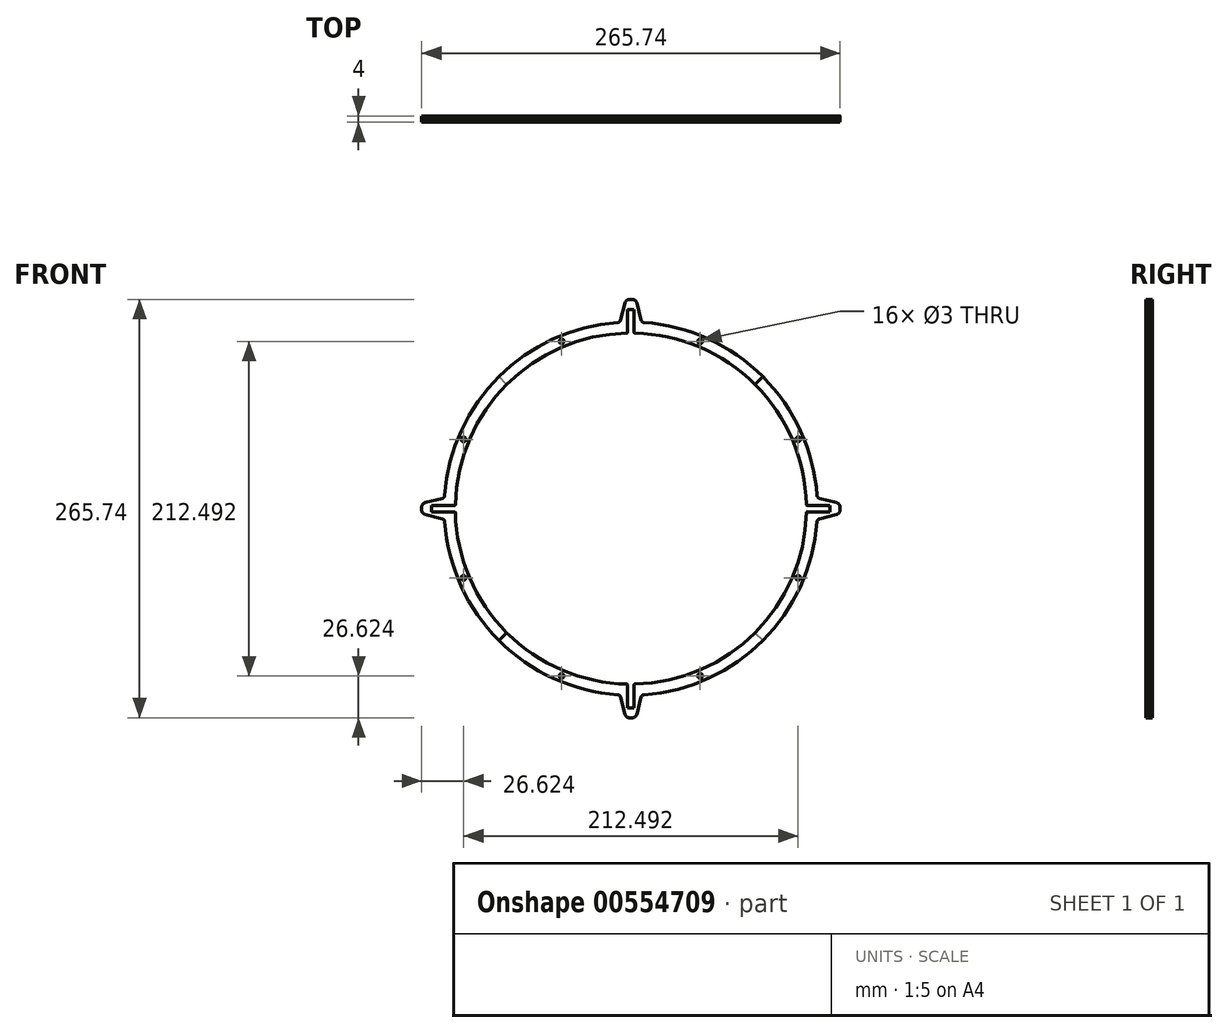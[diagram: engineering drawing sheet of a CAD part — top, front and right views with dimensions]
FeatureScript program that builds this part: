
annotation { "Feature Type Name" : "Feature", "Feature Type Description" : "" }
export const myFeature = defineFeature(function(context is Context, id is Id, definition is map)
    precondition{}
    {
        {
            var Q0;
            Q0=qCreatedBy(makeId("Front.planeOp"),FACE);
            var sketch = newSketch(context, id + "F0", { "sketchPlane" : qUnion([Q0])});
            skArc(sketch, "E0", {"start": v(-2.53, 111.47) * mm, "mid": v(-43.83, 102.52) * mm, "end": v(-78.84, 78.84) * mm});
            skArc(sketch, "E1", {"start": v(-8.32, 118.2) * mm, "mid": v(-49.16, 107.82) * mm, "end": v(-83.8, 83.8) * mm});
            skLineSegment(sketch, "E2", {"start": v(0, 0) * mm, "end": v(0, 308.78) * mm, "construction": true});
            skLineSegment(sketch, "E3", {"start": v(0, 0) * mm, "end": v(-78.84, 78.84) * mm, "construction": true});
            skLineSegment(sketch, "E4.bottom", {"start": v(0, 126.5) * mm, "end": v(2.18, 126.5) * mm});
            skLineSegment(sketch, "E5.bottom", {"start": v(-0.88, 132.87) * mm, "end": v(0.88, 132.87) * mm});
            skPoint(sketch, "E5.middle", {"position": v(0, 118.5) * mm});
            skLineSegment(sketch, "E6", {"start": v(-3.8, 130.6) * mm, "end": v(-6.52, 119.72) * mm});
            skLineSegment(sketch, "E7.MirrorCS", {"start": v(3.8, 130.6) * mm, "end": v(6.52, 119.72) * mm});
            skPoint(sketch, "E8.visualSharp", {"position": v(-3.23, 132.87) * mm});
            skArc(sketch, "E8.filletArc", {"start": v(-0.88, 132.87) * mm, "mid": v(-2.73, 132.23) * mm, "end": v(-3.8, 130.6) * mm});
            skPoint(sketch, "E9.visualSharp", {"position": v(3.23, 132.87) * mm});
            skArc(sketch, "E9.filletArc", {"start": v(3.8, 130.6) * mm, "mid": v(2.73, 132.23) * mm, "end": v(0.88, 132.87) * mm});
            skPoint(sketch, "E10.visualSharp", {"position": v(-1.55, 111.49) * mm});
            skPoint(sketch, "E11.visualSharp", {"position": v(1.55, 111.49) * mm});
            skPoint(sketch, "E12.visualSharp", {"position": v(-6.87, 118.3) * mm});
            skArc(sketch, "E12.filletArc", {"start": v(-8.32, 118.2) * mm, "mid": v(-7.17, 118.67) * mm, "end": v(-6.52, 119.72) * mm});
            skPoint(sketch, "E13.visualSharp", {"position": v(6.87, 118.3) * mm});
            skArc(sketch, "E13.filletArc", {"start": v(6.52, 119.72) * mm, "mid": v(7.17, 118.67) * mm, "end": v(8.32, 118.2) * mm});
            skLineSegment(sketch, "E14", {"start": v(0, 0) * mm, "end": v(-42.67, 103.01) * mm, "construction": true});
            skArc(sketch, "E15", {"start": v(83.8, 83.8) * mm, "mid": v(49.16, 107.82) * mm, "end": v(8.32, 118.2) * mm});
            skLineSegment(sketch, "E16", {"start": v(78.84, 78.84) * mm, "end": v(204.66, 204.66) * mm, "construction": true});
            skLineSegment(sketch, "E17", {"start": v(-83.8, 83.8) * mm, "end": v(-276.7, 276.7) * mm, "construction": true});
            skLineSegment(sketch, "E18", {"start": v(-78.84, 78.84) * mm, "end": v(-83.8, 83.8) * mm, "construction": true});
            skArc(sketch, "E19.trimOffspring", {"start": v(78.84, 78.84) * mm, "mid": v(43.83, 102.52) * mm, "end": v(2.53, 111.47) * mm});
            skLineSegment(sketch, "E20.3.6", {"start": v(78.84, 78.84) * mm, "end": v(83.8, 83.8) * mm, "construction": true});
            skPoint(sketch, "E21", {"position": v(-44, 106.25) * mm});
            skCircle(sketch, "E22", {"center": v(-44, 106.25) * mm, "radius": 1.5 * mm});
            skCircle(sketch, "E23.7.0", {"center": v(44, 106.25) * mm, "radius": 1.5 * mm});
            skLineSegment(sketch, "E24", {"start": v(83.8, 83.8) * mm, "end": v(78.84, 78.84) * mm});
            skLineSegment(sketch, "E25", {"start": v(-83.8, 83.8) * mm, "end": v(-78.84, 78.84) * mm});
            skPoint(sketch, "E26.orphan", {"position": v(-0.92, 126.5) * mm});
            skLineSegment(sketch, "E27.bottom", {"start": v(-2.05, 126.5) * mm, "end": v(2.05, 126.5) * mm});
            skLineSegment(sketch, "E27.left", {"start": v(-2.05, 126.5) * mm, "end": v(-2.05, 111.97) * mm});
            skLineSegment(sketch, "E27.right", {"start": v(2.05, 126.5) * mm, "end": v(2.05, 111.97) * mm});
            skLineSegment(sketch, "E28", {"start": v(-2.53, 111.47) * mm, "end": v(-2.52, 111.47) * mm});
            skPoint(sketch, "E29.visualSharp", {"position": v(-2.05, 111.5) * mm});
            skArc(sketch, "E29.filletArc", {"start": v(-2.52, 111.47) * mm, "mid": v(-2.19, 111.63) * mm, "end": v(-2.05, 111.97) * mm});
            skLineSegment(sketch, "E30.MirrorCS", {"start": v(2.53, 111.47) * mm, "end": v(2.52, 111.47) * mm});
            skArc(sketch, "E31.MirrorCS", {"start": v(2.52, 111.47) * mm, "mid": v(2.19, 111.63) * mm, "end": v(2.05, 111.97) * mm});
            skPoint(sketch, "E32.MirrorP", {"position": v(2.05, 111.5) * mm});
            skLineSegment(sketch, "E33.trimOffspring", {"start": v(-45.35, 109.48) * mm, "end": v(-110.65, 267.13) * mm, "construction": true});
            skPoint(sketch, "E34.1.0", {"position": v(-126.5, -0.92) * mm});
            skArc(sketch, "E34.1.1", {"start": v(-78.84, 78.84) * mm, "mid": v(-102.52, 43.83) * mm, "end": v(-111.47, 2.53) * mm});
            skPoint(sketch, "E34.1.2", {"position": v(-111.49, -1.55) * mm});
            skArc(sketch, "E34.1.3", {"start": v(-111.47, -2.53) * mm, "mid": v(-102.52, -43.83) * mm, "end": v(-78.84, -78.84) * mm});
            skPoint(sketch, "E34.1.4", {"position": v(-118.3, -6.87) * mm});
            skPoint(sketch, "E34.1.5", {"position": v(-111.5, 2.05) * mm});
            skPoint(sketch, "E34.1.6", {"position": v(-118.5, 0) * mm});
            skPoint(sketch, "E34.1.7", {"position": v(-111.5, -2.05) * mm});
            skPoint(sketch, "E34.1.8", {"position": v(-132.87, -3.23) * mm});
            skPoint(sketch, "E34.1.9", {"position": v(-111.49, 1.55) * mm});
            skArc(sketch, "E34.1.10", {"start": v(-118.2, -8.32) * mm, "mid": v(-107.82, -49.16) * mm, "end": v(-83.8, -83.8) * mm});
            skPoint(sketch, "E34.1.11", {"position": v(-132.87, 3.23) * mm});
            skPoint(sketch, "E34.1.12", {"position": v(-106.25, -44) * mm});
            skArc(sketch, "E34.1.13", {"start": v(-83.8, 83.8) * mm, "mid": v(-107.82, 49.16) * mm, "end": v(-118.2, 8.32) * mm});
            skPoint(sketch, "E34.1.14", {"position": v(-118.3, 6.87) * mm});
            skLineSegment(sketch, "E34.1.15", {"start": v(-126.5, -2.05) * mm, "end": v(-111.97, -2.05) * mm});
            skPoint(sketch, "E34.1.16", {"position": v(-111.49, 1.55) * mm});
            skCircle(sketch, "E34.1.17", {"center": v(-106.25, 44) * mm, "radius": 1.5 * mm});
            skLineSegment(sketch, "E34.1.18", {"start": v(-130.6, 3.8) * mm, "end": v(-119.72, 6.52) * mm});
            skLineSegment(sketch, "E34.1.19", {"start": v(-126.5, 2.05) * mm, "end": v(-111.97, 2.05) * mm});
            skLineSegment(sketch, "E34.1.20", {"start": v(-130.6, -3.8) * mm, "end": v(-119.72, -6.52) * mm});
            skCircle(sketch, "E34.1.21", {"center": v(-106.25, -44) * mm, "radius": 1.5 * mm});
            skLineSegment(sketch, "E34.1.22", {"start": v(-132.87, -0.88) * mm, "end": v(-132.87, 0.88) * mm});
            skArc(sketch, "E34.1.23", {"start": v(-118.2, -8.32) * mm, "mid": v(-118.67, -7.17) * mm, "end": v(-119.72, -6.52) * mm});
            skArc(sketch, "E34.1.24", {"start": v(-130.6, 3.8) * mm, "mid": v(-132.23, 2.73) * mm, "end": v(-132.87, 0.88) * mm});
            skArc(sketch, "E34.1.25", {"start": v(-132.87, -0.88) * mm, "mid": v(-132.23, -2.73) * mm, "end": v(-130.6, -3.8) * mm});
            skArc(sketch, "E34.1.26", {"start": v(-119.72, 6.52) * mm, "mid": v(-118.67, 7.17) * mm, "end": v(-118.2, 8.32) * mm});
            skLineSegment(sketch, "E34.1.28", {"start": v(-126.5, -2.05) * mm, "end": v(-126.5, 2.05) * mm});
            skLineSegment(sketch, "E34.1.29", {"start": v(-126.5, 0) * mm, "end": v(-126.5, 2.18) * mm});
            skLineSegment(sketch, "E34.1.30", {"start": v(-78.84, -78.84) * mm, "end": v(-83.8, -83.8) * mm, "construction": true});
            skLineSegment(sketch, "E34.1.32", {"start": v(-78.84, -78.84) * mm, "end": v(-83.8, -83.8) * mm, "construction": true});
            skLineSegment(sketch, "E34.1.34", {"start": v(-83.8, -83.8) * mm, "end": v(-78.84, -78.84) * mm});
            skArc(sketch, "E34.1.35", {"start": v(-111.47, -2.52) * mm, "mid": v(-111.63, -2.19) * mm, "end": v(-111.97, -2.05) * mm});
            skLineSegment(sketch, "E34.1.36", {"start": v(-111.47, -2.53) * mm, "end": v(-111.47, -2.52) * mm});
            skArc(sketch, "E34.1.37", {"start": v(-111.47, 2.52) * mm, "mid": v(-111.63, 2.19) * mm, "end": v(-111.97, 2.05) * mm});
            skLineSegment(sketch, "E34.1.38", {"start": v(-111.47, 2.53) * mm, "end": v(-111.47, 2.52) * mm});
            skPoint(sketch, "E34.2.0", {"position": v(0.92, -126.5) * mm});
            skArc(sketch, "E34.2.1", {"start": v(-78.84, -78.84) * mm, "mid": v(-43.83, -102.52) * mm, "end": v(-2.53, -111.47) * mm});
            skPoint(sketch, "E34.2.2", {"position": v(1.55, -111.49) * mm});
            skArc(sketch, "E34.2.3", {"start": v(2.53, -111.47) * mm, "mid": v(43.83, -102.52) * mm, "end": v(78.84, -78.84) * mm});
            skPoint(sketch, "E34.2.4", {"position": v(6.87, -118.3) * mm});
            skPoint(sketch, "E34.2.5", {"position": v(-2.05, -111.5) * mm});
            skPoint(sketch, "E34.2.6", {"position": v(0, -118.5) * mm});
            skPoint(sketch, "E34.2.7", {"position": v(2.05, -111.5) * mm});
            skPoint(sketch, "E34.2.8", {"position": v(3.23, -132.87) * mm});
            skPoint(sketch, "E34.2.9", {"position": v(-1.55, -111.49) * mm});
            skArc(sketch, "E34.2.10", {"start": v(8.32, -118.2) * mm, "mid": v(49.16, -107.82) * mm, "end": v(83.8, -83.8) * mm});
            skPoint(sketch, "E34.2.11", {"position": v(-3.23, -132.87) * mm});
            skPoint(sketch, "E34.2.12", {"position": v(44, -106.25) * mm});
            skArc(sketch, "E34.2.13", {"start": v(-83.8, -83.8) * mm, "mid": v(-49.16, -107.82) * mm, "end": v(-8.32, -118.2) * mm});
            skPoint(sketch, "E34.2.14", {"position": v(-6.87, -118.3) * mm});
            skLineSegment(sketch, "E34.2.15", {"start": v(2.05, -126.5) * mm, "end": v(2.05, -111.97) * mm});
            skPoint(sketch, "E34.2.16", {"position": v(-1.55, -111.49) * mm});
            skCircle(sketch, "E34.2.17", {"center": v(-44, -106.25) * mm, "radius": 1.5 * mm});
            skLineSegment(sketch, "E34.2.18", {"start": v(-3.8, -130.6) * mm, "end": v(-6.52, -119.72) * mm});
            skLineSegment(sketch, "E34.2.19", {"start": v(-2.05, -126.5) * mm, "end": v(-2.05, -111.97) * mm});
            skLineSegment(sketch, "E34.2.20", {"start": v(3.8, -130.6) * mm, "end": v(6.52, -119.72) * mm});
            skCircle(sketch, "E34.2.21", {"center": v(44, -106.25) * mm, "radius": 1.5 * mm});
            skLineSegment(sketch, "E34.2.22", {"start": v(0.88, -132.87) * mm, "end": v(-0.88, -132.87) * mm});
            skArc(sketch, "E34.2.23", {"start": v(8.32, -118.2) * mm, "mid": v(7.17, -118.67) * mm, "end": v(6.52, -119.72) * mm});
            skArc(sketch, "E34.2.24", {"start": v(-3.8, -130.6) * mm, "mid": v(-2.73, -132.23) * mm, "end": v(-0.88, -132.87) * mm});
            skArc(sketch, "E34.2.25", {"start": v(0.88, -132.87) * mm, "mid": v(2.73, -132.23) * mm, "end": v(3.8, -130.6) * mm});
            skArc(sketch, "E34.2.26", {"start": v(-6.52, -119.72) * mm, "mid": v(-7.17, -118.67) * mm, "end": v(-8.32, -118.2) * mm});
            skLineSegment(sketch, "E34.2.27", {"start": v(-78.84, -78.84) * mm, "end": v(-83.8, -83.8) * mm, "construction": true});
            skLineSegment(sketch, "E34.2.28", {"start": v(2.05, -126.5) * mm, "end": v(-2.05, -126.5) * mm});
            skLineSegment(sketch, "E34.2.29", {"start": v(0, -126.5) * mm, "end": v(-2.18, -126.5) * mm});
            skLineSegment(sketch, "E34.2.30", {"start": v(78.84, -78.84) * mm, "end": v(83.8, -83.8) * mm, "construction": true});
            skLineSegment(sketch, "E34.2.31", {"start": v(-83.8, -83.8) * mm, "end": v(-78.84, -78.84) * mm});
            skLineSegment(sketch, "E34.2.32", {"start": v(78.84, -78.84) * mm, "end": v(83.8, -83.8) * mm, "construction": true});
            skLineSegment(sketch, "E34.2.33", {"start": v(-83.8, -83.8) * mm, "end": v(-78.84, -78.84) * mm});
            skLineSegment(sketch, "E34.2.34", {"start": v(83.8, -83.8) * mm, "end": v(78.84, -78.84) * mm});
            skArc(sketch, "E34.2.35", {"start": v(2.52, -111.47) * mm, "mid": v(2.19, -111.63) * mm, "end": v(2.05, -111.97) * mm});
            skLineSegment(sketch, "E34.2.36", {"start": v(2.53, -111.47) * mm, "end": v(2.52, -111.47) * mm});
            skArc(sketch, "E34.2.37", {"start": v(-2.52, -111.47) * mm, "mid": v(-2.19, -111.63) * mm, "end": v(-2.05, -111.97) * mm});
            skLineSegment(sketch, "E34.2.38", {"start": v(-2.53, -111.47) * mm, "end": v(-2.52, -111.47) * mm});
            skPoint(sketch, "E34.3.0", {"position": v(126.5, 0.92) * mm});
            skArc(sketch, "E34.3.1", {"start": v(78.84, -78.84) * mm, "mid": v(102.52, -43.83) * mm, "end": v(111.47, -2.53) * mm});
            skPoint(sketch, "E34.3.2", {"position": v(111.49, 1.55) * mm});
            skArc(sketch, "E34.3.3", {"start": v(111.47, 2.53) * mm, "mid": v(102.52, 43.83) * mm, "end": v(78.84, 78.84) * mm});
            skPoint(sketch, "E34.3.4", {"position": v(118.3, 6.87) * mm});
            skPoint(sketch, "E34.3.5", {"position": v(111.5, -2.05) * mm});
            skPoint(sketch, "E34.3.6", {"position": v(118.5, 0) * mm});
            skPoint(sketch, "E34.3.7", {"position": v(111.5, 2.05) * mm});
            skPoint(sketch, "E34.3.8", {"position": v(132.87, 3.23) * mm});
            skPoint(sketch, "E34.3.9", {"position": v(111.49, -1.55) * mm});
            skArc(sketch, "E34.3.10", {"start": v(118.2, 8.32) * mm, "mid": v(107.82, 49.16) * mm, "end": v(83.8, 83.8) * mm});
            skPoint(sketch, "E34.3.11", {"position": v(132.87, -3.23) * mm});
            skPoint(sketch, "E34.3.12", {"position": v(106.25, 44) * mm});
            skArc(sketch, "E34.3.13", {"start": v(83.8, -83.8) * mm, "mid": v(107.82, -49.16) * mm, "end": v(118.2, -8.32) * mm});
            skPoint(sketch, "E34.3.14", {"position": v(118.3, -6.87) * mm});
            skLineSegment(sketch, "E34.3.15", {"start": v(126.5, 2.05) * mm, "end": v(111.97, 2.05) * mm});
            skPoint(sketch, "E34.3.16", {"position": v(111.49, -1.55) * mm});
            skCircle(sketch, "E34.3.17", {"center": v(106.25, -44) * mm, "radius": 1.5 * mm});
            skLineSegment(sketch, "E34.3.18", {"start": v(130.6, -3.8) * mm, "end": v(119.72, -6.52) * mm});
            skLineSegment(sketch, "E34.3.19", {"start": v(126.5, -2.05) * mm, "end": v(111.97, -2.05) * mm});
            skLineSegment(sketch, "E34.3.20", {"start": v(130.6, 3.8) * mm, "end": v(119.72, 6.52) * mm});
            skCircle(sketch, "E34.3.21", {"center": v(106.25, 44) * mm, "radius": 1.5 * mm});
            skLineSegment(sketch, "E34.3.22", {"start": v(132.87, 0.88) * mm, "end": v(132.87, -0.88) * mm});
            skArc(sketch, "E34.3.23", {"start": v(118.2, 8.32) * mm, "mid": v(118.67, 7.17) * mm, "end": v(119.72, 6.52) * mm});
            skArc(sketch, "E34.3.24", {"start": v(130.6, -3.8) * mm, "mid": v(132.23, -2.73) * mm, "end": v(132.87, -0.88) * mm});
            skArc(sketch, "E34.3.25", {"start": v(132.87, 0.88) * mm, "mid": v(132.23, 2.73) * mm, "end": v(130.6, 3.8) * mm});
            skArc(sketch, "E34.3.26", {"start": v(119.72, -6.52) * mm, "mid": v(118.67, -7.17) * mm, "end": v(118.2, -8.32) * mm});
            skLineSegment(sketch, "E34.3.27", {"start": v(78.84, -78.84) * mm, "end": v(83.8, -83.8) * mm, "construction": true});
            skLineSegment(sketch, "E34.3.28", {"start": v(126.5, 2.05) * mm, "end": v(126.5, -2.05) * mm});
            skLineSegment(sketch, "E34.3.29", {"start": v(126.5, 0) * mm, "end": v(126.5, -2.18) * mm});
            skLineSegment(sketch, "E34.3.31", {"start": v(83.8, -83.8) * mm, "end": v(78.84, -78.84) * mm});
            skLineSegment(sketch, "E34.3.33", {"start": v(83.8, -83.8) * mm, "end": v(78.84, -78.84) * mm});
            skArc(sketch, "E34.3.35", {"start": v(111.47, 2.52) * mm, "mid": v(111.63, 2.19) * mm, "end": v(111.97, 2.05) * mm});
            skLineSegment(sketch, "E34.3.36", {"start": v(111.47, 2.53) * mm, "end": v(111.47, 2.52) * mm});
            skArc(sketch, "E34.3.37", {"start": v(111.47, -2.52) * mm, "mid": v(111.63, -2.19) * mm, "end": v(111.97, -2.05) * mm});
            skLineSegment(sketch, "E34.3.38", {"start": v(111.47, -2.53) * mm, "end": v(111.47, -2.52) * mm});
            skSolve(sketch);
        }
        {
            var Q0;
            Q0=makeQuery(id+"F0.imprint","IMPRINT",FACE,{"disambiguationData":[TD([[makeQuery(id+"F0.imprint","IMPRINT",EDGE,{"derivedFrom":sQuery(id+"F0.wireOp",EDGE,"E34.1.1")}),-1.0]])]});
            var Q1;
            Q1=makeQuery(id+"F0.imprint","IMPRINT",FACE,{"disambiguationData":[TD([[makeQuery(id+"F0.imprint","IMPRINT",EDGE,{"derivedFrom":sQuery(id+"F0.wireOp",EDGE,"E0")}),-1.0]])]});
            extrude(context, id + "F1", {"entities" : qUnion([Q0, Q1]), "depth" : 2 * mm, "offsetDistance" : 25 * mm});
        }
        {
            var Q0;
            Q0=makeQuery(id+"F0.imprint","IMPRINT",FACE,{"disambiguationData":[TD([[makeQuery(id+"F0.imprint","IMPRINT",EDGE,{"derivedFrom":sQuery(id+"F0.wireOp",EDGE,"E34.3.1")}),-1.0]])]});
            var Q1;
            Q1=makeQuery(id+"F0.imprint","IMPRINT",FACE,{"disambiguationData":[TD([[makeQuery(id+"F0.imprint","IMPRINT",EDGE,{"derivedFrom":sQuery(id+"F0.wireOp",EDGE,"E34.2.1")}),-1.0]])]});
            extrude(context, id + "F2", {"entities" : qUnion([Q0, Q1]), "depth" : 2 * mm, "offsetDistance" : 25 * mm});
        }
        {
            var Q0;
            Q0=makeQuery(id+"F0.imprint","IMPRINT",FACE,{"disambiguationData":[TD([[makeQuery(id+"F0.imprint","IMPRINT",EDGE,{"derivedFrom":sQuery(id+"F0.wireOp",EDGE,"E0")}),-1.0]])]});
            var Q1;
            Q1=makeQuery(id+"F0.imprint","IMPRINT",FACE,{"disambiguationData":[TD([[makeQuery(id+"F0.imprint","IMPRINT",EDGE,{"derivedFrom":sQuery(id+"F0.wireOp",EDGE,"E34.3.1")}),-1.0]])]});
            extrude(context, id + "F3", {"entities" : qUnion([Q0, Q1]), "oppositeDirection" : true, "depth" : 2 * mm, "offsetDistance" : 25 * mm});
        }
        {
            var Q0;
            Q0=makeQuery(id+"F0.imprint","IMPRINT",FACE,{"disambiguationData":[TD([[makeQuery(id+"F0.imprint","IMPRINT",EDGE,{"derivedFrom":sQuery(id+"F0.wireOp",EDGE,"E34.1.1")}),-1.0]])]});
            var Q1;
            Q1=makeQuery(id+"F0.imprint","IMPRINT",FACE,{"disambiguationData":[TD([[makeQuery(id+"F0.imprint","IMPRINT",EDGE,{"derivedFrom":sQuery(id+"F0.wireOp",EDGE,"E34.2.1")}),-1.0]])]});
            extrude(context, id + "F4", {"entities" : qUnion([Q0, Q1]), "oppositeDirection" : true, "depth" : 2 * mm, "offsetDistance" : 25 * mm});
        }
    });
